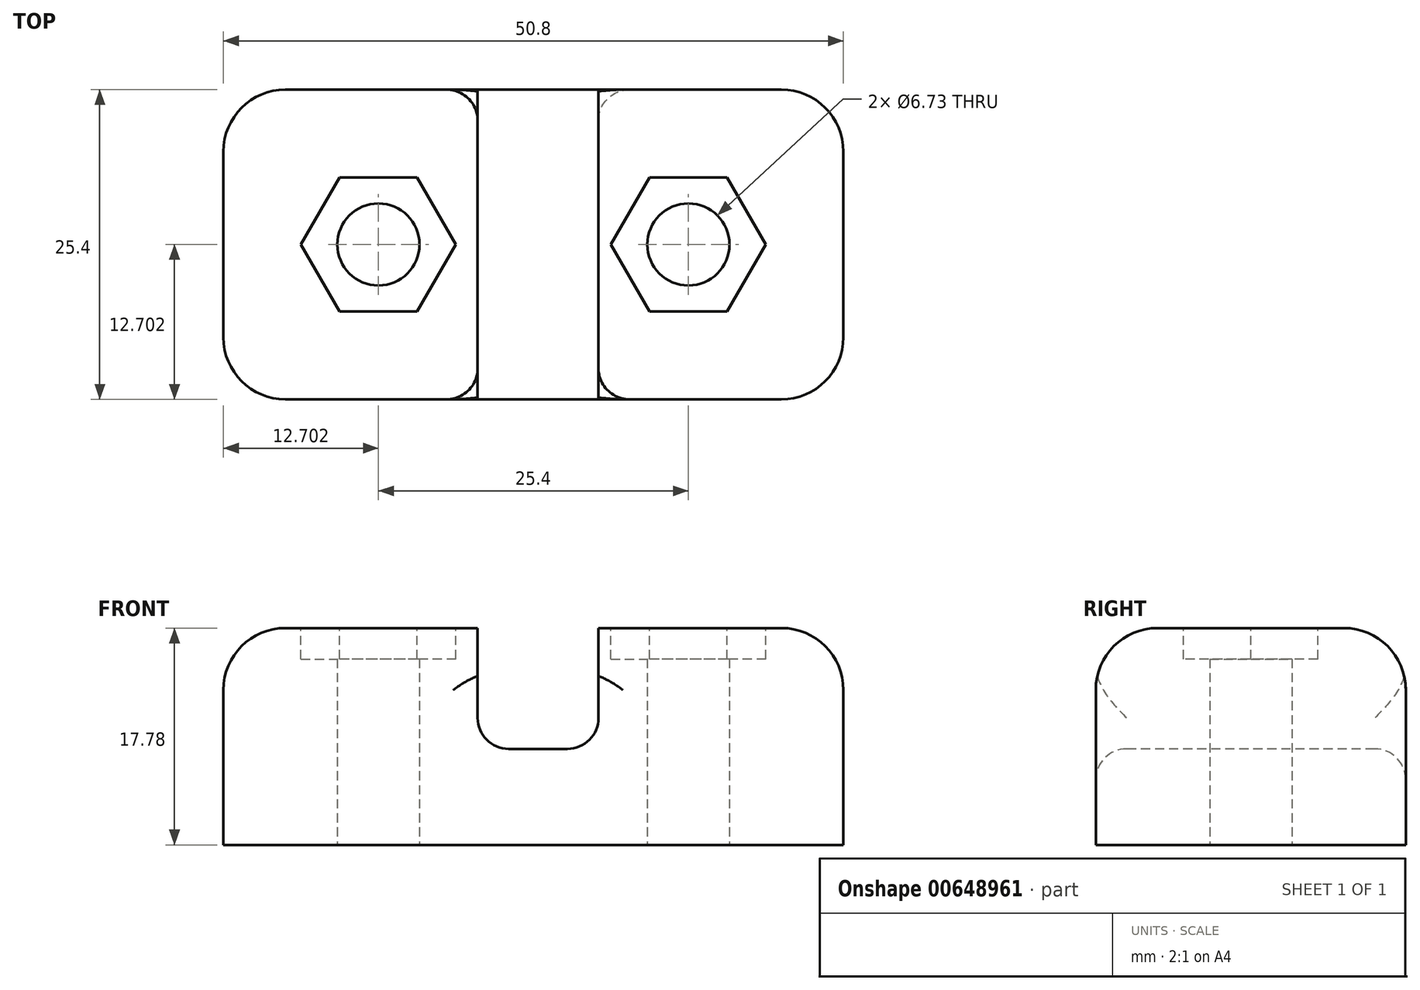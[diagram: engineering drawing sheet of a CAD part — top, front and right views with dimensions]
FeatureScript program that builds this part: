
annotation { "Feature Type Name" : "Feature", "Feature Type Description" : "" }
export const myFeature = defineFeature(function(context is Context, id is Id, definition is map)
    precondition{}
    {
        {
            var Q0;
            Q0=qCreatedBy(makeId("Top.planeOp"),FACE);
            var sketch = newSketch(context, id + "F0", { "sketchPlane" : qUnion([Q0])});
            skLineSegment(sketch, "E0.bottom", {"start": v(-5.24, 8.9) * mm, "end": v(45.56, 8.9) * mm});
            skLineSegment(sketch, "E0.top", {"start": v(-5.24, -16.5) * mm, "end": v(45.56, -16.5) * mm});
            skLineSegment(sketch, "E0.left", {"start": v(-5.24, 8.9) * mm, "end": v(-5.24, -16.5) * mm});
            skLineSegment(sketch, "E0.right", {"start": v(45.56, 8.9) * mm, "end": v(45.56, -16.5) * mm});
            skCircle(sketch, "E1", {"center": v(32.86, -3.8) * mm, "radius": 3.37 * mm});
            skCircle(sketch, "E2", {"center": v(7.46, -3.8) * mm, "radius": 3.37 * mm});
            skSolve(sketch);
        }
        {
            var Q0;
            Q0=makeQuery(id+"F0.imprint","IMPRINT",FACE,{"disambiguationData":[TD([[makeQuery(id+"F0.imprint","IMPRINT",EDGE,{"derivedFrom":sQuery(id+"F0.wireOp",EDGE,"E1")}),-1.0]])]});
            var Q1;
            Q1=makeQuery(id+"F0.imprint","IMPRINT",FACE,{"disambiguationData":[TD([[makeQuery(id+"F0.imprint","IMPRINT",EDGE,{"derivedFrom":sQuery(id+"F0.wireOp",EDGE,"E2")}),-1.0]])]});
            var Q2;
            Q2=makeQuery(id+"F0.imprint","IMPRINT",FACE,{"disambiguationData":[TD([[makeQuery(id+"F0.imprint","IMPRINT",EDGE,{"derivedFrom":sQuery(id+"F0.wireOp",EDGE,"E0.bottom")}),-1.0]])]});
            extrude(context, id + "F1", {"entities" : qUnion([Q0, Q1, Q2]), "depth" : 17.78 * mm, "offsetDistance" : 25.4 * mm});
        }
        {
            var Q0;
            Q0=makeQuery(id+"F1.opExtrude","CAP_FACE",FACE,{"disambiguationData":[OSD([sQuery(id+"F0.wireOp",EDGE,"E0.bottom"),sQuery(id+"F0.wireOp",EDGE,"E0.top"),sQuery(id+"F0.wireOp",EDGE,"E0.left"),sQuery(id+"F0.wireOp",EDGE,"E0.right"),sQuery(id+"F0.wireOp",EDGE,"fUYtTBID-xgAi-ahwc-gfW2-qXiPDuYIcXCT"),sQuery(id+"F0.wireOp",EDGE,"E1")])],"isStart":false});
            var sketch = newSketch(context, id + "F2", { "sketchPlane" : qUnion([Q0])});
            skLineSegment(sketch, "E3.bottom", {"start": v(15.6, 8.9) * mm, "end": v(25.5, 8.9) * mm});
            skLineSegment(sketch, "E3.top", {"start": v(15.6, -16.5) * mm, "end": v(25.5, -16.5) * mm});
            skLineSegment(sketch, "E3.left", {"start": v(15.6, 8.9) * mm, "end": v(15.6, -16.5) * mm});
            skLineSegment(sketch, "E3.right", {"start": v(25.5, 8.9) * mm, "end": v(25.5, -16.5) * mm});
            skSolve(sketch);
        }
        {
            var Q0;
            Q0=makeQuery(id+"F2.imprint","IMPRINT",FACE,{"disambiguationData":[TD([[makeQuery(id+"F2.imprint","IMPRINT",EDGE,{"derivedFrom":sQuery(id+"F2.wireOp",EDGE,"E3.bottom")}),-1.0]])]});
            extrude(context, id + "F3", {"entities" : qUnion([Q0]), "operationType" : NewBodyOperationType.REMOVE, "oppositeDirection" : true, "depth" : 9.9 * mm, "offsetDistance" : 25.4 * mm});
        }
        {
            var Q0;
            {var subQ0=sQuery(id+"F0.wireOp",EDGE,"E0.right");var subQ1=sQuery(id+"F0.wireOp",EDGE,"E0.bottom");var subQ2=sQuery(id+"F0.wireOp",EDGE,"E1");var subQ3=sQuery(id+"F0.wireOp",EDGE,"E0.top");Q0=makeQuery(id+"F3.boolean.opBoolean","SPLIT",FACE,{"disambiguationData":[TD([makeQuery(id+"F1.opExtrude","SWEPT_FACE",FACE,{"disambiguationData":[OSD([subQ3])]})])],"derivedFrom":makeQuery(id+"F1.opExtrude","CAP_FACE",FACE,{"disambiguationData":[OSD([subQ1,subQ3,sQuery(id+"F0.wireOp",EDGE,"E0.left"),subQ0,subQ2])],"isStart":false})});}
            var sketch = newSketch(context, id + "F4", { "sketchPlane" : qUnion([Q0])});
            skCircle(sketch, "E4.cCircle", {"center": v(32.86, -3.8) * mm, "radius": 6.35 * mm, "construction": true});
            skLineSegment(sketch, "E4.0", {"start": v(36.04, -9.3) * mm, "end": v(29.69, -9.3) * mm});
            skLineSegment(sketch, "E4.1", {"start": v(29.69, -9.3) * mm, "end": v(26.51, -3.8) * mm});
            skLineSegment(sketch, "E4.2", {"start": v(26.51, -3.8) * mm, "end": v(29.69, 1.7) * mm});
            skLineSegment(sketch, "E4.3", {"start": v(29.69, 1.7) * mm, "end": v(36.04, 1.7) * mm});
            skLineSegment(sketch, "E4.4", {"start": v(36.04, 1.7) * mm, "end": v(39.21, -3.8) * mm});
            skLineSegment(sketch, "E4.5", {"start": v(39.21, -3.8) * mm, "end": v(36.04, -9.3) * mm});
            skCircle(sketch, "E5.cCircle", {"center": v(7.46, -3.8) * mm, "radius": 6.35 * mm, "construction": true});
            skLineSegment(sketch, "E5.0", {"start": v(10.64, -9.3) * mm, "end": v(4.29, -9.3) * mm});
            skLineSegment(sketch, "E5.1", {"start": v(4.29, -9.3) * mm, "end": v(1.11, -3.8) * mm});
            skLineSegment(sketch, "E5.2", {"start": v(1.11, -3.8) * mm, "end": v(4.29, 1.7) * mm});
            skLineSegment(sketch, "E5.3", {"start": v(4.29, 1.7) * mm, "end": v(10.64, 1.7) * mm});
            skLineSegment(sketch, "E5.4", {"start": v(10.64, 1.7) * mm, "end": v(13.81, -3.8) * mm});
            skLineSegment(sketch, "E5.5", {"start": v(13.81, -3.8) * mm, "end": v(10.64, -9.3) * mm});
            skSolve(sketch);
        }
        {
            var Q0;
            Q0 = qSketchRegion(id + "F4", true);
            extrude(context, id + "F5", {"entities" : qUnion([Q0]), "operationType" : NewBodyOperationType.REMOVE, "oppositeDirection" : true, "depth" : 2.54 * mm, "offsetDistance" : 25.4 * mm});
        }
        {
            var Q0;
            Q0=makeQuery(id+"F1.opExtrude","CAP_EDGE",EDGE,{"disambiguationData":[OSD([sQuery(id+"F0.wireOp",EDGE,"E0.right")])],"isStart":false});
            var Q1;
            {var subQ0=sQuery(id+"F0.wireOp",EDGE,"E0.bottom");var subQ1=sQuery(id+"F0.wireOp",EDGE,"E0.left");Q1=makeQuery(id+"F3.boolean.opBoolean","SPLIT",EDGE,{"disambiguationData":[TD([makeQuery(id+"F1.opExtrude","SWEPT_FACE",FACE,{"disambiguationData":[OSD([subQ1])]})])],"derivedFrom":makeQuery(id+"F1.opExtrude","CAP_EDGE",EDGE,{"disambiguationData":[OSD([subQ0])],"isStart":false})});}
            var Q2;
            Q2=makeQuery(id+"F1.opExtrude","CAP_EDGE",EDGE,{"disambiguationData":[OSD([sQuery(id+"F0.wireOp",EDGE,"E0.left")])],"isStart":false});
            var Q3;
            Q3=makeQuery(id+"F3.boolean.opBoolean","COPY",EDGE,{"derivedFrom":makeQuery(id+"F3.opExtrude","CAP_EDGE",EDGE,{"disambiguationData":[OSD([sQuery(id+"F2.wireOp",EDGE,"DSloTTO4-oqDd-6Mfo-KRlK-PVZZl6v1pi03")])],"isStart":true})});
            var Q4;
            Q4=makeQuery(id+"F3.boolean.opBoolean","COPY",EDGE,{"derivedFrom":makeQuery(id+"F3.opExtrude","CAP_EDGE",EDGE,{"disambiguationData":[OSD([sQuery(id+"F2.wireOp",EDGE,"RV5eaW5d-XTiz-xa95-bEWG-xIZ8fB0XSvS9")])],"isStart":true})});
            var Q5;
            {var subQ0=sQuery(id+"F0.wireOp",EDGE,"E0.left");var subQ1=sQuery(id+"F0.wireOp",EDGE,"E0.top");Q5=makeQuery(id+"F3.boolean.opBoolean","SPLIT",EDGE,{"disambiguationData":[TD([makeQuery(id+"F1.opExtrude","SWEPT_FACE",FACE,{"disambiguationData":[OSD([subQ0])]})])],"derivedFrom":makeQuery(id+"F1.opExtrude","CAP_EDGE",EDGE,{"disambiguationData":[OSD([subQ1])],"isStart":false})});}
            var Q6;
            {var subQ0=sQuery(id+"F0.wireOp",EDGE,"E0.right");var subQ1=sQuery(id+"F0.wireOp",EDGE,"E0.top");Q6=makeQuery(id+"F3.boolean.opBoolean","SPLIT",EDGE,{"disambiguationData":[TD([makeQuery(id+"F1.opExtrude","SWEPT_FACE",FACE,{"disambiguationData":[OSD([subQ0])]})])],"derivedFrom":makeQuery(id+"F1.opExtrude","CAP_EDGE",EDGE,{"disambiguationData":[OSD([subQ1])],"isStart":false})});}
            var Q7;
            {var subQ0=sQuery(id+"F0.wireOp",EDGE,"E0.bottom");var subQ1=sQuery(id+"F0.wireOp",EDGE,"E0.right");Q7=makeQuery(id+"F3.boolean.opBoolean","SPLIT",EDGE,{"disambiguationData":[TD([makeQuery(id+"F1.opExtrude","SWEPT_FACE",FACE,{"disambiguationData":[OSD([subQ1])]})])],"derivedFrom":makeQuery(id+"F1.opExtrude","CAP_EDGE",EDGE,{"disambiguationData":[OSD([subQ0])],"isStart":false})});}
            var Q8;
            Q8=makeQuery(id+"F1.opExtrude","SWEPT_EDGE",EDGE,{"disambiguationData":[OSD([sQuery(id+"F0.wireOp",EDGE,"E0.bottom"),sQuery(id+"F0.wireOp",EDGE,"E0.left")])]});
            var Q9;
            Q9=makeQuery(id+"F1.opExtrude","SWEPT_EDGE",EDGE,{"disambiguationData":[OSD([sQuery(id+"F0.wireOp",EDGE,"E0.top"),sQuery(id+"F0.wireOp",EDGE,"E0.left")])]});
            var Q10;
            Q10=makeQuery(id+"F1.opExtrude","SWEPT_EDGE",EDGE,{"disambiguationData":[OSD([sQuery(id+"F0.wireOp",EDGE,"E0.top"),sQuery(id+"F0.wireOp",EDGE,"E0.right")])]});
            var Q11;
            Q11=makeQuery(id+"F1.opExtrude","SWEPT_EDGE",EDGE,{"disambiguationData":[OSD([sQuery(id+"F0.wireOp",EDGE,"E0.bottom"),sQuery(id+"F0.wireOp",EDGE,"E0.right")])]});
            fillet(context, id + "F6", {"entities" : qUnion([Q0, Q1, Q2, Q3, Q4, Q5, Q6, Q7, Q8, Q9, Q10, Q11]), "radius" : 5.08 * mm, "tangentPropagation" : true, "allowEdgeOverflow" : false});
        }
        {
            var Q0;
            Q0=makeQuery(id+"F3.boolean.opBoolean","COPY",FACE,{"derivedFrom":makeQuery(id+"F3.opExtrude","CAP_FACE",FACE,{"disambiguationData":[OSD([sQuery(id+"F2.wireOp",EDGE,"E3.bottom"),sQuery(id+"F2.wireOp",EDGE,"E3.top"),sQuery(id+"F2.wireOp",EDGE,"E3.left"),sQuery(id+"F2.wireOp",EDGE,"E3.right")])],"isStart":false})});
            fillet(context, id + "F7", {"entities" : qUnion([Q0]), "radius" : 2.54 * mm, "tangentPropagation" : true, "allowEdgeOverflow" : false});
        }
    });
